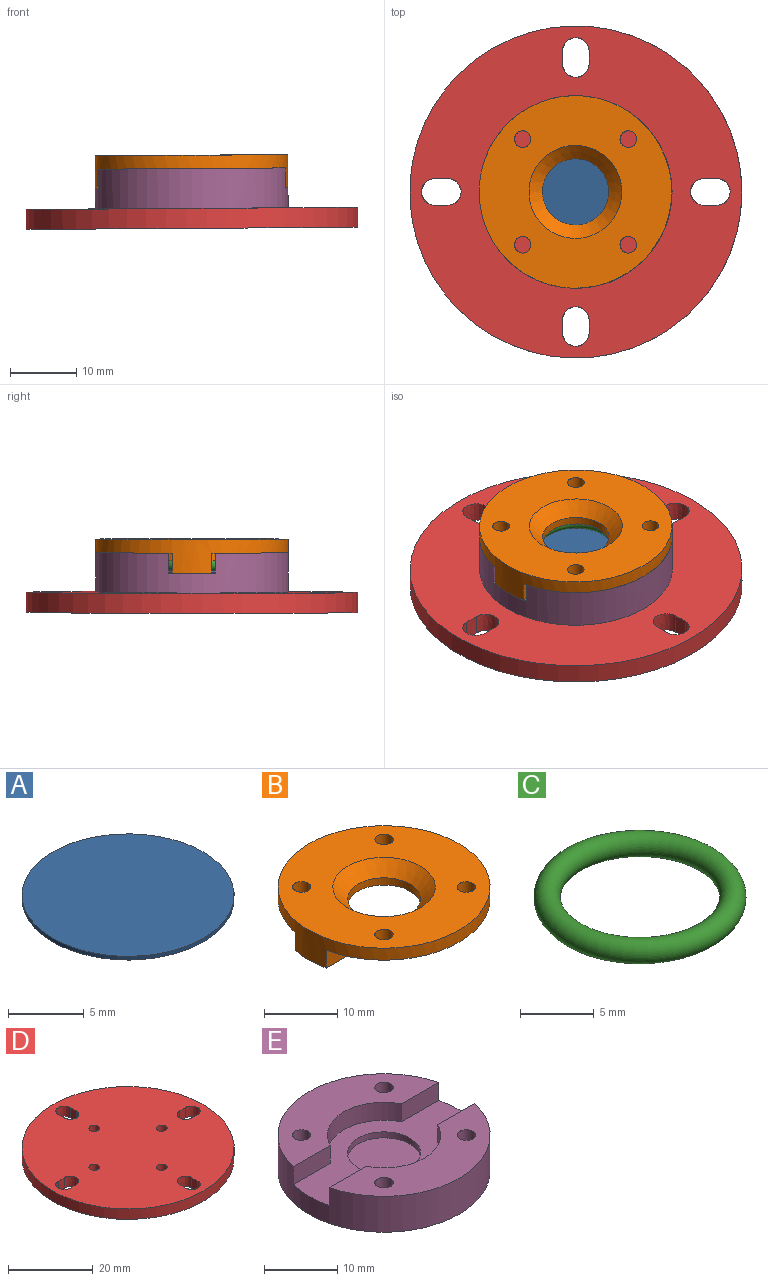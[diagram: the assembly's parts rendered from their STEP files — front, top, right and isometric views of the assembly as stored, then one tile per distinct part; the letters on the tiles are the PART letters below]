
ASSEMBLY  parts=5 mates=8
PART A: 3 faces, bbox 14x14x0.3 mm
  f0: cylinder r=7mm len=14mm, axis (0,0,-1), area 13.2mm2, adj f1,f2
  f1: plane 14x14mm, normal (0,0,1), area 153.9mm2, adj f0
  f2: plane 14x14mm, normal (0,0,-1), area 153.9mm2, adj f0
PART B: 21 faces, bbox 29x29x5 mm
  f0: cylinder r=7.5mm len=13.75mm, axis (0,0,1), area 20.9mm2, adj f3,f11,f12,f17
  f1: cylinder r=7.5mm len=13.75mm, axis (0,0,1), area 20.9mm2, adj f3,f8,f13,f16
  f2: cylinder r=5mm len=10mm, axis (0,0,1), area 37.7mm2, adj f3,f20
  f3: plane 15x15mm, normal (0,0,-1), area 98.2mm2, adj f0,f1,f2,f14,f18
  f4: plane 29x29mm, normal (0,0,1), area 486.9mm2, adj f5,f6,f7,f9,f10,f20
  f5: cylinder r=14.5mm len=29mm, axis (0,0,1), area 218.5mm2, adj f4,f8,f11,f12,f13,f15,f16,f17
  f6: cylinder r=1.25mm len=2.5mm, axis (0,0,1), area 15.7mm2, adj f4,f8
  f7: cylinder r=1.25mm len=2.5mm, axis (0,0,1), area 15.7mm2, adj f4,f8
  f8: plane 28.37x11.5mm, normal (0,0,-1), area 189.5mm2, adj f1,f5,f6,f7,f13,f16
  f9: cylinder r=1.25mm len=2.5mm, axis (0,0,1), area 15.7mm2, adj f4,f11
  f10: cylinder r=1.25mm len=2.5mm, axis (0,0,1), area 15.7mm2, adj f4,f11
  f11: plane 28.37x11.5mm, normal (0,0,-1), area 189.5mm2, adj f0,f5,f9,f10,f12,f17
  f12: plane 7.31x3mm, normal (0,1,0), area 21.9mm2, adj f0,f5,f11,f14,f15
  f13: plane 7.31x3mm, normal (0,-1,0), area 21.9mm2, adj f1,f5,f8,f14,f15
  f14: cylinder r=7.5mm len=6mm, axis (0,0,1), area 11.1mm2, adj f3,f12,f13,f15
  f15: plane 7.63x6mm, normal (0,0,-1), area 42.6mm2, adj f5,f12,f13,f14
  f16: plane 7.31x3mm, normal (0,-1,0), area 21.9mm2, adj f1,f5,f8,f18,f19
  f17: plane 7.31x3mm, normal (0,1,0), area 21.9mm2, adj f0,f5,f11,f18,f19
  f18: cylinder r=7.5mm len=6mm, axis (0,0,1), area 11.1mm2, adj f3,f16,f17,f19
  f19: plane 7.63x6mm, normal (0,0,-1), area 42.6mm2, adj f5,f16,f17,f18
  f20: cone r=7mm half-angle=45deg, axis (0,0,1), area 106.6mm2, adj f2,f4
PART C: 1 faces, bbox 15.5x15.5x1.8 mm
  f0: torus R=6.29mm, axis (0,0,-1), area 221mm2
PART D: 23 faces, bbox 50x50x3 mm
  f0: plane 3x2mm, normal (-1,0,0), area 6mm2, adj f1,f20,f21,f22
  f1: extruded ~4x3mm, area 18.8mm2, adj f0,f2,f21,f22
  f2: plane 3x2mm, normal (1,0,0), area 6mm2, adj f1,f20,f21,f22
  f3: plane 3x2mm, normal (1,0,0), area 6mm2, adj f4,f17,f21,f22
  f4: extruded ~4x3mm, area 18.8mm2, adj f3,f5,f21,f22
  f5: plane 3x2mm, normal (-1,0,0), area 6mm2, adj f4,f17,f21,f22
  f6: extruded ~4x3mm, area 18.8mm2, adj f7,f18,f21,f22
  f7: plane 3x2mm, normal (0,1,0), area 6mm2, adj f6,f8,f21,f22
  f8: extruded ~4x3mm, area 18.8mm2, adj f7,f18,f21,f22
  f9: plane 3x2mm, normal (0,-1,0), area 6mm2, adj f10,f19,f21,f22
  f10: extruded ~4x3mm, area 18.8mm2, adj f9,f11,f21,f22
  f11: plane 3x2mm, normal (0,1,0), area 6mm2, adj f10,f19,f21,f22
  f12: cylinder r=25mm len=50mm, axis (0,0,-1), area 471.2mm2, adj f21,f22
  f13: cylinder r=1.25mm len=3mm, axis (0,0,-1), area 23.6mm2, adj f21,f22
  f14: cylinder r=1.25mm len=3mm, axis (0,0,-1), area 23.6mm2, adj f21,f22
  f15: cylinder r=1.25mm len=3mm, axis (0,0,-1), area 23.6mm2, adj f21,f22
  f16: cylinder r=1.25mm len=3mm, axis (0,0,-1), area 23.6mm2, adj f21,f22
  f17: extruded ~4x3mm, area 18.8mm2, adj f3,f5,f21,f22
  f18: plane 3x2mm, normal (0,-1,0), area 6mm2, adj f6,f8,f21,f22
  f19: extruded ~4x3mm, area 18.8mm2, adj f9,f11,f21,f22
  f20: extruded ~4x3mm, area 18.8mm2, adj f0,f2,f21,f22
  f21: plane 50x50mm, normal (0,0,1), area 1861.6mm2, adj f0,f1,f2,f3,f4,f5,f6,f7
  f22: plane 50x50mm, normal (0,0,-1), area 1861.6mm2, adj f0,f1,f2,f3,f4,f5,f6,f7
PART E: 17 faces, bbox 29x29x6 mm
  f0: cylinder r=14.5mm len=29mm, axis (0,0,-1), area 504.2mm2, adj f2,f3,f4,f5,f9,f10,f11,f15
  f1: cylinder r=5mm len=10mm, axis (0,0,-1), area 31.4mm2, adj f2,f16
  f2: plane 29x15.5mm, normal (0,0,1), area 206.5mm2, adj f0,f1,f4,f5,f6,f10,f11,f12
  f3: plane 29x29mm, normal (0,0,-1), area 640.9mm2, adj f0,f7,f8,f13,f14
  f4: plane 7.16x3mm, normal (0,-1,0), area 21.5mm2, adj f0,f2,f6,f9
  f5: plane 7.16x3mm, normal (0,-1,0), area 21.5mm2, adj f0,f2,f6,f9
  f6: cylinder r=7.75mm len=13.83mm, axis (0,0,-1), area 51.3mm2, adj f2,f4,f5,f9
  f7: cylinder r=1.25mm len=6mm, axis (0,0,-1), area 47.1mm2, adj f3,f9
  f8: cylinder r=1.25mm len=6mm, axis (0,0,-1), area 47.1mm2, adj f3,f9
  f9: plane 28.14x11mm, normal (0,0,1), area 177.9mm2, adj f0,f4,f5,f6,f7,f8
  f10: plane 7.16x3mm, normal (0,1,0), area 21.5mm2, adj f0,f2,f12,f15
  f11: plane 7.16x3mm, normal (0,1,0), area 21.5mm2, adj f0,f2,f12,f15
  f12: cylinder r=7.75mm len=13.83mm, axis (0,0,-1), area 51.3mm2, adj f2,f10,f11,f15
  f13: cylinder r=1.25mm len=6mm, axis (0,0,-1), area 47.1mm2, adj f3,f15
  f14: cylinder r=1.25mm len=6mm, axis (0,0,-1), area 47.1mm2, adj f3,f15
  f15: plane 28.14x11mm, normal (0,0,1), area 177.9mm2, adj f0,f10,f11,f12,f13,f14
  f16: plane 10x10mm, normal (0,0,1), area 78.5mm2, adj f1
PLACE A rot(axis=(0.07,-1,0),0.4deg) t=(-9.35,20.81,-18)mm
PLACE B rot(axis=(0.07,-1,0.01),0.4deg) t=(-9.39,20.8,-13)mm
PLACE C rot(axis=(0.07,-1,0.01),0.4deg) t=(-9.36,20.81,-16.81)mm
PLACE D rot(axis=(0.07,-1,0),0.4deg) t=(-9.31,20.81,-24)mm
PLACE E rot(axis=(0.07,-1,0),0.4deg) t=(-9.33,20.81,-21)mm
MATE cylindrical A.f0 <-> E.f0  axis (-0.01,0,1) through (-9.35,20.81,-17.7)mm
MATE planar C.f0 <-> A.f0  axis (0.01,0,-1) through (-9.36,20.81,-16.81)mm
MATE planar A.f0 <-> E.f1  axis (0.01,0,-1) through (-9.35,20.81,-18)mm
MATE cylindrical B.f5 <-> A.f0  axis (-0.01,0,1) through (-9.39,20.8,-13)mm
MATE planar E.f0 <-> D.f12  axis (0.01,0,-1) through (-9.33,20.81,-21)mm
MATE cylindrical C.f0 <-> A.f0  axis (0.01,0,-1) through (-9.36,20.81,-16.81)mm
MATE cylindrical E.f0 <-> D.f12  axis (0.01,0,-1) through (-9.33,20.81,-21)mm
MATE planar B.f11 <-> E.f9  axis (0.01,0,-1) through (-9.37,29.29,-15)mm
